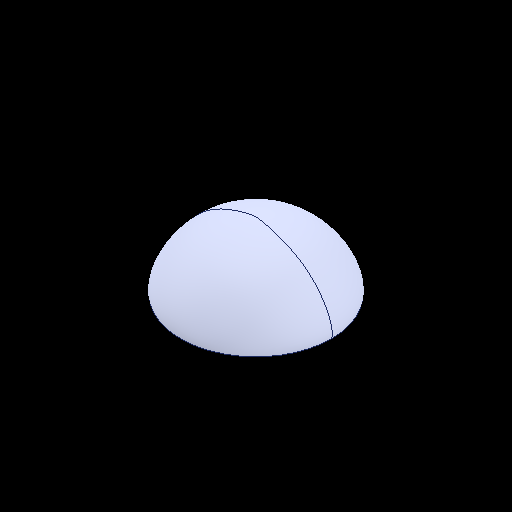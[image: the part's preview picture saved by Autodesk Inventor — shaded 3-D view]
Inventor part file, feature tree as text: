
AUTODESK INVENTOR PART (.ipt)
format: ipt  version: 2022 (Build 260153000, 153)  size: 121,856 bytes
history: native  units: in
note: dims shown in document units (in); Inventor stores cm internally (conversion verified against a paired STEP export)
features: revolve x1
ambient origin geometry x8: Origin, YZ Plane, XZ Plane, XY Plane, X Axis, Y Axis, Z Axis, Center Point
bodies: Solid1 (feature_tree)
feature tree (1):
  revolve  "Revolve1"  [1 undecoded]
note: 1 required parameter value undecoded (feature->parameter linkage not recoverable at this tier; creation-order binding heuristic only, values carry confidence <= 0.55)
